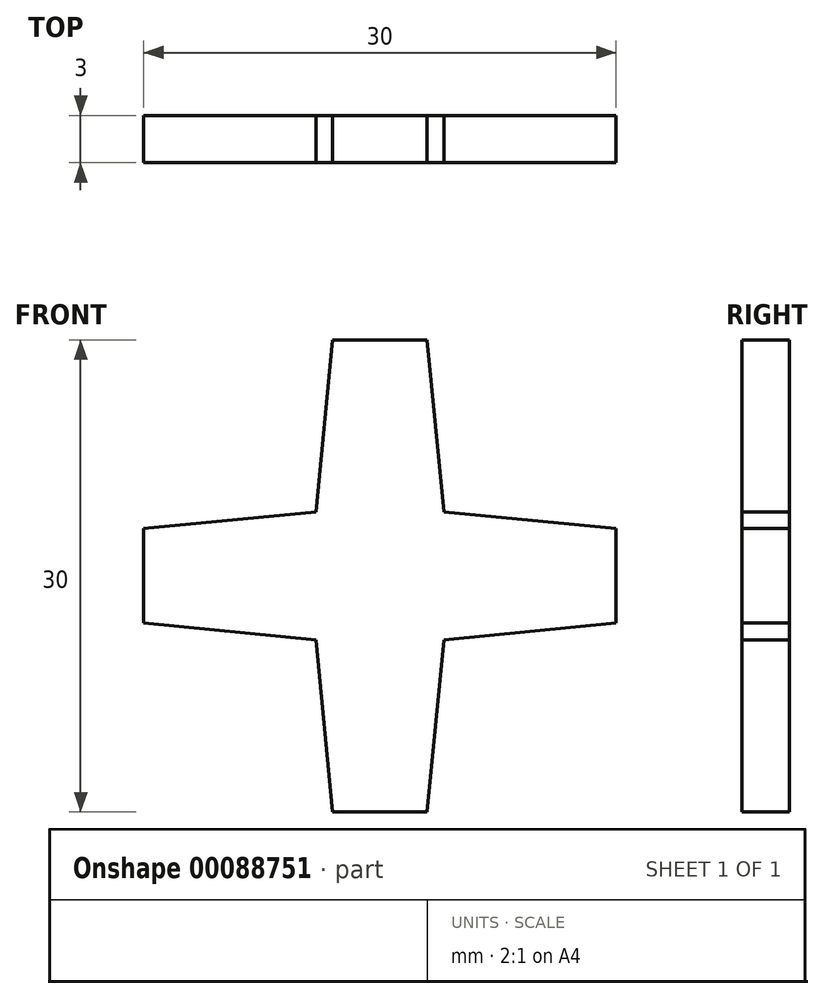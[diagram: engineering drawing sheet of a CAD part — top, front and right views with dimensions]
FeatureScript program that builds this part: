
annotation { "Feature Type Name" : "Feature", "Feature Type Description" : "" }
export const myFeature = defineFeature(function(context is Context, id is Id, definition is map)
    precondition{}
    {
        {
            var Q0;
            Q0=qCreatedBy(makeId("Front.planeOp"),FACE);
            var sketch = newSketch(context, id + "F0", { "sketchPlane" : qUnion([Q0])});
            skLineSegment(sketch, "E0", {"start": v(0, 0) * mm, "end": v(15, 0) * mm, "construction": true});
            skLineSegment(sketch, "E1", {"start": v(0, 0) * mm, "end": v(0, 15) * mm, "construction": true});
            skLineSegment(sketch, "E2", {"start": v(0, 15) * mm, "end": v(3, 15) * mm});
            skLineSegment(sketch, "E3", {"start": v(15, 0) * mm, "end": v(15, 3) * mm});
            skLineSegment(sketch, "E4", {"start": v(3, 15) * mm, "end": v(4.05, 4.05) * mm});
            skLineSegment(sketch, "E5", {"start": v(4.05, 4.05) * mm, "end": v(15, 3) * mm});
            skLineSegment(sketch, "E6", {"start": v(4.05, 4.05) * mm, "end": v(0, 0) * mm, "construction": true});
            skLineSegment(sketch, "E7.MirrorCS", {"start": v(0, 15) * mm, "end": v(-3, 15) * mm});
            skLineSegment(sketch, "E8.MirrorCS", {"start": v(0, 0) * mm, "end": v(-15, 0) * mm, "construction": true});
            skLineSegment(sketch, "E9.MirrorCS", {"start": v(-4.05, 4.05) * mm, "end": v(0, 0) * mm, "construction": true});
            skLineSegment(sketch, "E10.MirrorCS", {"start": v(-15, 0) * mm, "end": v(-15, 3) * mm});
            skLineSegment(sketch, "E11.MirrorCS", {"start": v(-3, 15) * mm, "end": v(-4.05, 4.05) * mm});
            skLineSegment(sketch, "E12.MirrorCS", {"start": v(-4.05, 4.05) * mm, "end": v(-15, 3) * mm});
            skLineSegment(sketch, "E13.MirrorCS", {"start": v(0, 0) * mm, "end": v(0, -15) * mm, "construction": true});
            skLineSegment(sketch, "E14.MirrorCS", {"start": v(4.05, -4.05) * mm, "end": v(15, -3) * mm});
            skLineSegment(sketch, "E15.MirrorCS", {"start": v(0, -15) * mm, "end": v(3, -15) * mm});
            skLineSegment(sketch, "E16.MirrorCS", {"start": v(4.05, -4.05) * mm, "end": v(0, 0) * mm, "construction": true});
            skLineSegment(sketch, "E17.MirrorCS", {"start": v(3, -15) * mm, "end": v(4.05, -4.05) * mm});
            skLineSegment(sketch, "E18.MirrorCS", {"start": v(-4.05, -4.05) * mm, "end": v(0, 0) * mm, "construction": true});
            skLineSegment(sketch, "E19.MirrorCS", {"start": v(0, -15) * mm, "end": v(-3, -15) * mm});
            skLineSegment(sketch, "E20.MirrorCS", {"start": v(-4.05, -4.05) * mm, "end": v(-15, -3) * mm});
            skLineSegment(sketch, "E21.MirrorCS", {"start": v(-3, -15) * mm, "end": v(-4.05, -4.05) * mm});
            skLineSegment(sketch, "E22.MirrorCS", {"start": v(-15, 0) * mm, "end": v(-15, -3) * mm});
            skLineSegment(sketch, "E23.MirrorCS", {"start": v(15, 0) * mm, "end": v(15, -3) * mm});
            skSolve(sketch);
        }
        {
            var Q0;
            Q0 = qSketchRegion(id + "F0", true);
            extrude(context, id + "F1", {"entities" : qUnion([Q0]), "depth" : 3 * mm});
        }
    });
